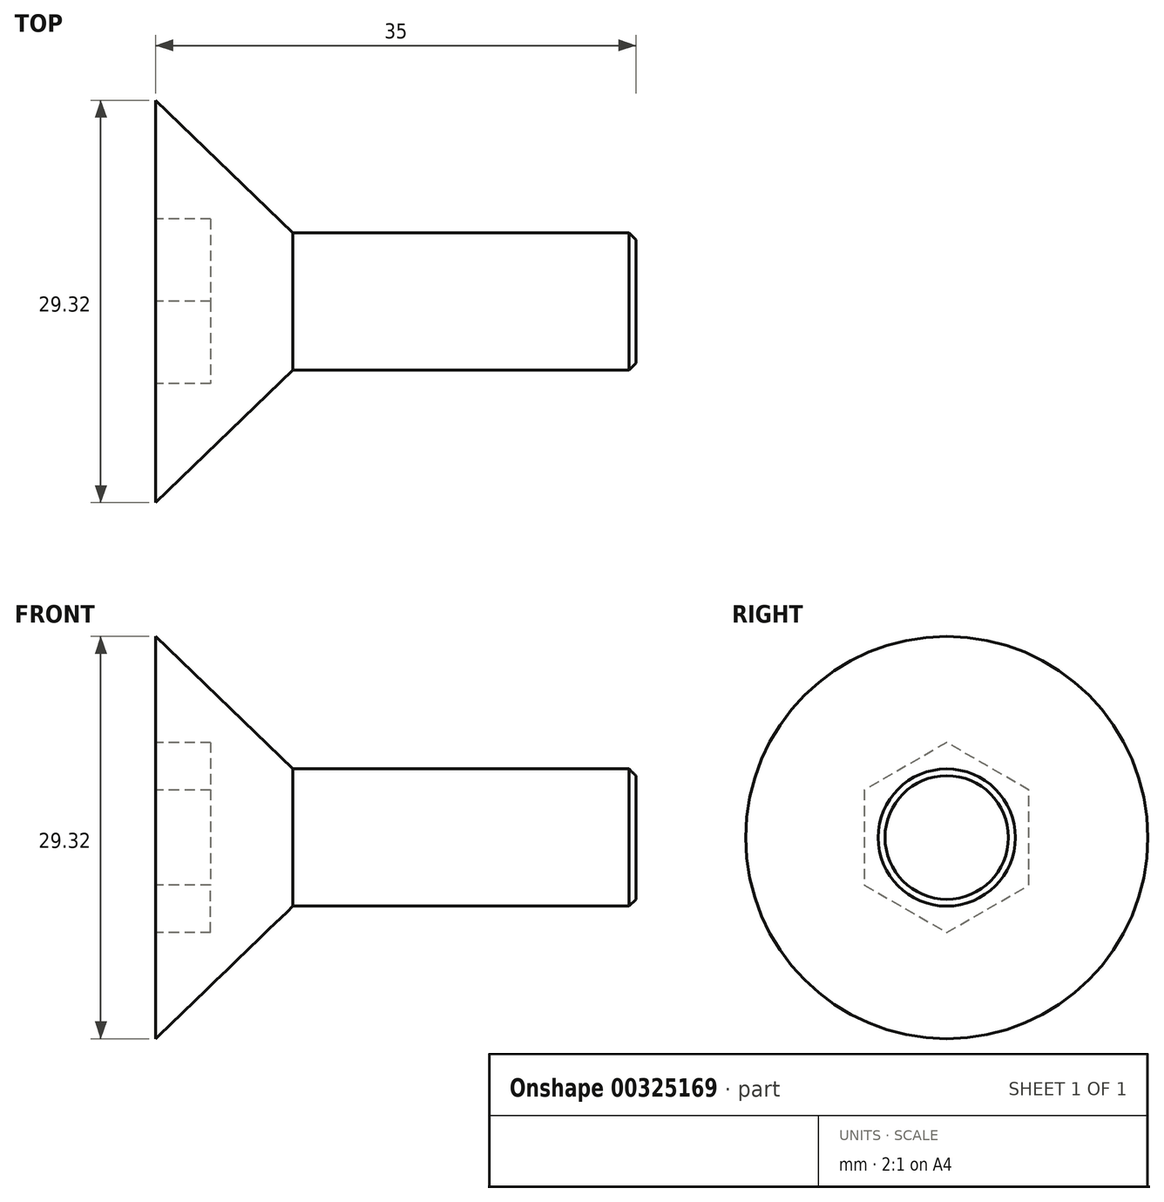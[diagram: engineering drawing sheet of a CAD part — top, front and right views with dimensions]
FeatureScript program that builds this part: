
annotation { "Feature Type Name" : "Feature", "Feature Type Description" : "" }
export const myFeature = defineFeature(function(context is Context, id is Id, definition is map)
    precondition{}
    {
        {
            var Q0;
            Q0=qCreatedBy(makeId("Front.planeOp"),FACE);
            var sketch = newSketch(context, id + "F0", { "sketchPlane" : qUnion([Q0])});
            skLineSegment(sketch, "E0", {"start": v(0, 0) * mm, "end": v(0, 14.66) * mm});
            skLineSegment(sketch, "E1", {"start": v(0, 14.66) * mm, "end": v(10, 5) * mm});
            skLineSegment(sketch, "E2", {"start": v(10, 5) * mm, "end": v(35, 5) * mm});
            skLineSegment(sketch, "E3", {"start": v(35, 5) * mm, "end": v(35, 0) * mm});
            skLineSegment(sketch, "E4", {"start": v(35, 0) * mm, "end": v(0, 0) * mm});
            skLineSegment(sketch, "E5", {"start": v(35, 0) * mm, "end": v(41.86, 0) * mm, "construction": true});
            skSolve(sketch);
        }
        {
            var Q0;
            Q0=makeQuery(id+"F0.imprint","IMPRINT",FACE,{"disambiguationData":[TD([[makeQuery(id+"F0.imprint","IMPRINT",EDGE,{"derivedFrom":sQuery(id+"F0.wireOp",EDGE,"E0")}),-1.0]])]});
            var Q1;
            Q1=sQuery(id+"F0.wireOp",EDGE,"E4");
            revolve(context, id + "F1", {"entities" : qUnion([Q0]), "axis" : qUnion([Q1]), "revolveType" : RevolveType.FULL});
        }
        {
            var Q0;
            Q0=makeQuery(id+"F1.opRevolve","SWEPT_FACE",FACE,{"disambiguationData":[OSD([sQuery(id+"F0.wireOp",EDGE,"E0")])]});
            var sketch = newSketch(context, id + "F2", { "sketchPlane" : qUnion([Q0])});
            skCircle(sketch, "E6.cCircle", {"center": v(0, 0) * mm, "radius": 6 * mm, "construction": true});
            skLineSegment(sketch, "E6.0", {"start": v(6, 3.46) * mm, "end": v(6, -3.46) * mm});
            skLineSegment(sketch, "E6.1", {"start": v(6, -3.46) * mm, "end": v(0, -6.93) * mm});
            skLineSegment(sketch, "E6.2", {"start": v(0, -6.93) * mm, "end": v(-6, -3.46) * mm});
            skLineSegment(sketch, "E6.3", {"start": v(-6, -3.46) * mm, "end": v(-6, 3.46) * mm});
            skLineSegment(sketch, "E6.4", {"start": v(-6, 3.46) * mm, "end": v(0, 6.93) * mm});
            skLineSegment(sketch, "E6.5", {"start": v(0, 6.93) * mm, "end": v(6, 3.46) * mm});
            skPoint(sketch, "E6.0.midPoint", {"position": v(6, 0) * mm});
            skSolve(sketch);
        }
        {
            var Q0;
            Q0=makeQuery(id+"F2.imprint","IMPRINT",FACE,{"disambiguationData":[TD([[makeQuery(id+"F2.imprint","IMPRINT",EDGE,{"derivedFrom":sQuery(id+"F2.wireOp",EDGE,"E6.0")}),-1.0]])]});
            extrude(context, id + "F3", {"entities" : qUnion([Q0]), "operationType" : NewBodyOperationType.REMOVE, "oppositeDirection" : true, "depth" : 4 * mm});
        }
        {
            var Q0;
            Q0=makeQuery(id+"F1.opRevolve","SWEPT_FACE",FACE,{"disambiguationData":[OSD([sQuery(id+"F0.wireOp",EDGE,"E3")])]});
            chamfer(context, id + "F4", {"entities" : qUnion([Q0]), "width" : 0.5 * mm, "tangentPropagation" : true});
        }
    });
